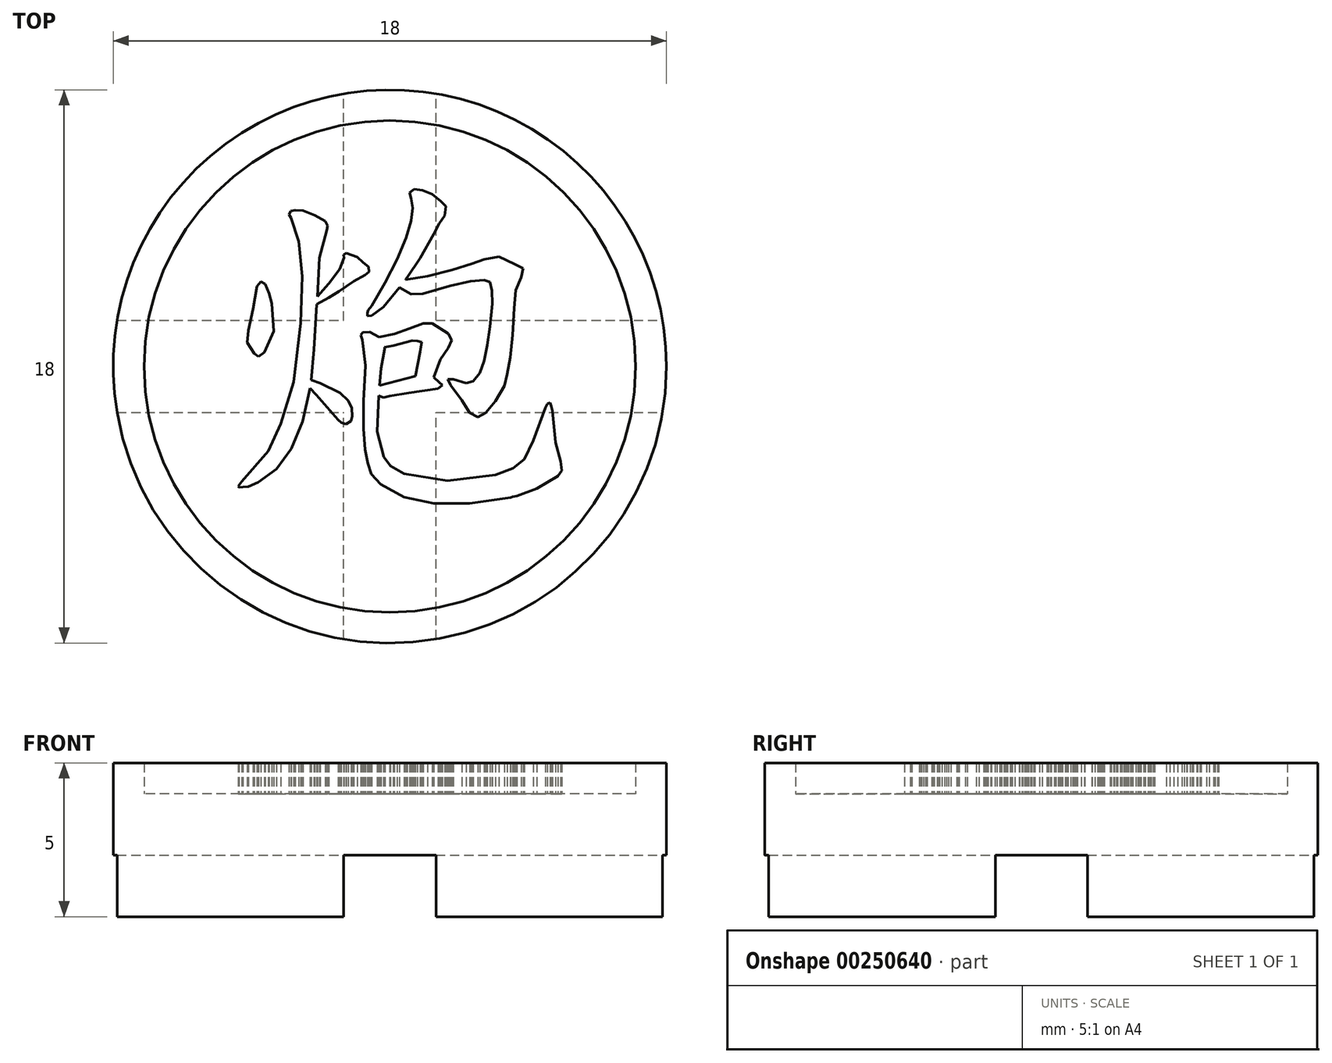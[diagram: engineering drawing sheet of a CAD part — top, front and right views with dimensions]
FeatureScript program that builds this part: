
annotation { "Feature Type Name" : "Feature", "Feature Type Description" : "" }
export const myFeature = defineFeature(function(context is Context, id is Id, definition is map)
    precondition{}
    {
        {
            var Q0;
            Q0=qCreatedBy(makeId("Top.planeOp"),FACE);
            var sketch = newSketch(context, id + "F0", { "sketchPlane" : qUnion([Q0])});
            skCircle(sketch, "E0", {"center": v(-31.33, 19.76) * mm, "radius": 9 * mm});
            skSolve(sketch);
        }
        {
            var Q0;
            Q0=qSketchRegion(id+"F0",true);
            extrude(context, id + "F1", {"entities" : qUnion([Q0]), "depth" : 4 * mm});
        }
        {
            var Q0;
            Q0=makeQuery(id+"F1.opExtrude","CAP_FACE",FACE,{"disambiguationData":[OSD([sQuery(id+"F0.wireOp",EDGE,"E0")])],"isStart":false});
            var sketch = newSketch(context, id + "F2", { "sketchPlane" : qUnion([Q0])});
            skCircle(sketch, "E1", {"center": v(-31.33, 19.76) * mm, "radius": 8 * mm});
            skCircle(sketch, "E2", {"center": v(-31.33, 19.76) * mm, "radius": 9 * mm});
            skSolve(sketch);
        }
        {
            var Q0;
            Q0=makeQuery(id+"F1.opExtrude","CAP_FACE",FACE,{"disambiguationData":[OSD([sQuery(id+"F0.wireOp",EDGE,"E0")])],"isStart":true});
            var sketch = newSketch(context, id + "F3", { "sketchPlane" : qUnion([Q0])});
            skLineSegment(sketch, "E3", {"start": v(-31.33, -19.76) * mm, "end": v(-22.33, -19.76) * mm, "construction": true});
            skLineSegment(sketch, "E4", {"start": v(-31.33, -19.76) * mm, "end": v(-31.33, -10.76) * mm, "construction": true});
            skLineSegment(sketch, "E5", {"start": v(-31.33, -19.76) * mm, "end": v(-40.33, -19.76) * mm, "construction": true});
            skLineSegment(sketch, "E6", {"start": v(-31.33, -19.76) * mm, "end": v(-31.33, -28.76) * mm, "construction": true});
            skLineSegment(sketch, "E7.bottom", {"start": v(-40.33, -28.76) * mm, "end": v(-22.33, -28.76) * mm});
            skLineSegment(sketch, "E7.top", {"start": v(-40.33, -10.76) * mm, "end": v(-22.33, -10.76) * mm});
            skLineSegment(sketch, "E7.left", {"start": v(-22.33, -10.76) * mm, "end": v(-22.33, -28.76) * mm});
            skLineSegment(sketch, "E7.right", {"start": v(-40.33, -10.76) * mm, "end": v(-40.33, -28.76) * mm});
            skPoint(sketch, "E8", {"position": v(-31.33, -28.76) * mm});
            skPoint(sketch, "E9", {"position": v(-40.33, -19.76) * mm});
            skPoint(sketch, "E10", {"position": v(-22.33, -19.76) * mm});
            skPoint(sketch, "E11", {"position": v(-31.33, -10.76) * mm});
            skLineSegment(sketch, "E12.bottom", {"start": v(-32.83, -10.76) * mm, "end": v(-29.83, -10.76) * mm});
            skLineSegment(sketch, "E12.top", {"start": v(-32.83, -28.76) * mm, "end": v(-29.83, -28.76) * mm});
            skLineSegment(sketch, "E12.left", {"start": v(-32.83, -10.76) * mm, "end": v(-32.83, -28.76) * mm});
            skLineSegment(sketch, "E12.right", {"start": v(-29.83, -10.76) * mm, "end": v(-29.83, -28.76) * mm});
            skLineSegment(sketch, "E13.bottom", {"start": v(-40.33, -18.26) * mm, "end": v(-22.33, -18.26) * mm});
            skLineSegment(sketch, "E13.top", {"start": v(-40.33, -21.26) * mm, "end": v(-22.33, -21.26) * mm});
            skLineSegment(sketch, "E13.left", {"start": v(-40.33, -18.26) * mm, "end": v(-40.33, -21.26) * mm});
            skLineSegment(sketch, "E13.right", {"start": v(-22.33, -18.26) * mm, "end": v(-22.33, -21.26) * mm});
            skSolve(sketch);
        }
        {
            var Q0;
            {var subQ1=sQuery(id+"F3.wireOp",EDGE,"E12.bottom");var subQ3=makeQuery(id+"F1.opExtrude","CAP_EDGE",EDGE,{"disambiguationData":[OSD([sQuery(id+"F0.wireOp",EDGE,"E0")])],"isStart":true});var subQ4=makeQuery(id+"F3.imprint","INTERSECT",VERTEX,{"derivedFrom":[subQ3,subQ1]});Q0=makeQuery(id+"F3.imprint","IMPRINT",FACE,{"disambiguationData":[TD([[makeQuery(id+"F3.imprint","IMPRINT",EDGE,{"disambiguationData":[TD([[subQ4,1.0]])],"derivedFrom":subQ3}),1.0]])]});}
            var Q1;
            {var subQ1=sQuery(id+"F3.wireOp",EDGE,"E12.bottom");var subQ3=makeQuery(id+"F1.opExtrude","CAP_EDGE",EDGE,{"disambiguationData":[OSD([sQuery(id+"F0.wireOp",EDGE,"E0")])],"isStart":true});var subQ4=makeQuery(id+"F3.imprint","INTERSECT",VERTEX,{"derivedFrom":[subQ3,subQ1]});Q1=makeQuery(id+"F3.imprint","IMPRINT",FACE,{"disambiguationData":[TD([[makeQuery(id+"F3.imprint","IMPRINT",EDGE,{"disambiguationData":[TD([[subQ4,-1.0]])],"derivedFrom":subQ3}),1.0]])]});}
            var Q2;
            {var subQ1=sQuery(id+"F3.wireOp",EDGE,"E12.top");var subQ3=makeQuery(id+"F1.opExtrude","CAP_EDGE",EDGE,{"disambiguationData":[OSD([sQuery(id+"F0.wireOp",EDGE,"E0")])],"isStart":true});var subQ4=makeQuery(id+"F3.imprint","INTERSECT",VERTEX,{"derivedFrom":[subQ3,subQ1]});Q2=makeQuery(id+"F3.imprint","IMPRINT",FACE,{"disambiguationData":[TD([[makeQuery(id+"F3.imprint","IMPRINT",EDGE,{"disambiguationData":[TD([[subQ4,-1.0]])],"derivedFrom":subQ3}),1.0]])]});}
            var Q3;
            {var subQ1=sQuery(id+"F3.wireOp",EDGE,"E12.top");var subQ3=makeQuery(id+"F1.opExtrude","CAP_EDGE",EDGE,{"disambiguationData":[OSD([sQuery(id+"F0.wireOp",EDGE,"E0")])],"isStart":true});var subQ4=makeQuery(id+"F3.imprint","INTERSECT",VERTEX,{"derivedFrom":[subQ3,subQ1]});Q3=makeQuery(id+"F3.imprint","IMPRINT",FACE,{"disambiguationData":[TD([[makeQuery(id+"F3.imprint","IMPRINT",EDGE,{"disambiguationData":[TD([[subQ4,1.0]])],"derivedFrom":subQ3}),1.0]])]});}
            var Q4;
            {var subQ0=sQuery(id+"F3.wireOp",EDGE,"E13.left");var subQ3=makeQuery(id+"F1.opExtrude","CAP_EDGE",EDGE,{"disambiguationData":[OSD([sQuery(id+"F0.wireOp",EDGE,"E0")])],"isStart":true});var subQ5=makeQuery(id+"F3.imprint","INTERSECT",VERTEX,{"derivedFrom":[subQ3,subQ0]});Q4=makeQuery(id+"F3.imprint","IMPRINT",FACE,{"disambiguationData":[TD([[makeQuery(id+"F3.imprint","IMPRINT",EDGE,{"disambiguationData":[TD([[subQ5,-1.0]])],"derivedFrom":subQ3}),1.0]])]});}
            var Q5;
            {var subQ0=sQuery(id+"F3.wireOp",EDGE,"E13.right");var subQ3=makeQuery(id+"F1.opExtrude","CAP_EDGE",EDGE,{"disambiguationData":[OSD([sQuery(id+"F0.wireOp",EDGE,"E0")])],"isStart":true});var subQ5=makeQuery(id+"F3.imprint","INTERSECT",VERTEX,{"derivedFrom":[subQ3,subQ0]});Q5=makeQuery(id+"F3.imprint","IMPRINT",FACE,{"disambiguationData":[TD([[makeQuery(id+"F3.imprint","IMPRINT",EDGE,{"disambiguationData":[TD([[subQ5,1.0]])],"derivedFrom":subQ3}),1.0]])]});}
            var Q6;
            {var subQ0=sQuery(id+"F3.wireOp",EDGE,"E13.left");var subQ3=makeQuery(id+"F1.opExtrude","CAP_EDGE",EDGE,{"disambiguationData":[OSD([sQuery(id+"F0.wireOp",EDGE,"E0")])],"isStart":true});var subQ5=makeQuery(id+"F3.imprint","INTERSECT",VERTEX,{"derivedFrom":[subQ3,subQ0]});Q6=makeQuery(id+"F3.imprint","IMPRINT",FACE,{"disambiguationData":[TD([[makeQuery(id+"F3.imprint","IMPRINT",EDGE,{"disambiguationData":[TD([[subQ5,1.0]])],"derivedFrom":subQ3}),1.0]])]});}
            var Q7;
            {var subQ0=sQuery(id+"F3.wireOp",EDGE,"E13.right");var subQ3=makeQuery(id+"F1.opExtrude","CAP_EDGE",EDGE,{"disambiguationData":[OSD([sQuery(id+"F0.wireOp",EDGE,"E0")])],"isStart":true});var subQ5=makeQuery(id+"F3.imprint","INTERSECT",VERTEX,{"derivedFrom":[subQ3,subQ0]});Q7=makeQuery(id+"F3.imprint","IMPRINT",FACE,{"disambiguationData":[TD([[makeQuery(id+"F3.imprint","IMPRINT",EDGE,{"disambiguationData":[TD([[subQ5,-1.0]])],"derivedFrom":subQ3}),1.0]])]});}
            var Q8;
            {var subQ3=makeQuery(id+"F1.opExtrude","CAP_EDGE",EDGE,{"disambiguationData":[OSD([sQuery(id+"F0.wireOp",EDGE,"E0")])],"isStart":true});var subQ5=sQuery(id+"F3.wireOp",EDGE,"E12.left");var subQ8=makeQuery(id+"F3.imprint","INTERSECT",VERTEX,{"disambiguationData":[OD(1.0)],"derivedFrom":[subQ3,subQ5]});Q8=makeQuery(id+"F3.imprint","IMPRINT",FACE,{"disambiguationData":[TD([[makeQuery(id+"F3.imprint","IMPRINT",EDGE,{"disambiguationData":[TD([[subQ8,-1.0]])],"derivedFrom":subQ3}),1.0]])]});}
            var Q9;
            {var subQ3=makeQuery(id+"F1.opExtrude","CAP_EDGE",EDGE,{"disambiguationData":[OSD([sQuery(id+"F0.wireOp",EDGE,"E0")])],"isStart":true});var subQ5=sQuery(id+"F3.wireOp",EDGE,"E12.right");var subQ8=makeQuery(id+"F3.imprint","INTERSECT",VERTEX,{"disambiguationData":[OD(1.0)],"derivedFrom":[subQ3,subQ5]});Q9=makeQuery(id+"F3.imprint","IMPRINT",FACE,{"disambiguationData":[TD([[makeQuery(id+"F3.imprint","IMPRINT",EDGE,{"disambiguationData":[TD([[subQ8,1.0]])],"derivedFrom":subQ3}),1.0]])]});}
            var Q10;
            {var subQ3=makeQuery(id+"F1.opExtrude","CAP_EDGE",EDGE,{"disambiguationData":[OSD([sQuery(id+"F0.wireOp",EDGE,"E0")])],"isStart":true});var subQ5=sQuery(id+"F3.wireOp",EDGE,"E12.left");var subQ8=makeQuery(id+"F3.imprint","INTERSECT",VERTEX,{"disambiguationData":[OD(0.0)],"derivedFrom":[subQ3,subQ5]});Q10=makeQuery(id+"F3.imprint","IMPRINT",FACE,{"disambiguationData":[TD([[makeQuery(id+"F3.imprint","IMPRINT",EDGE,{"disambiguationData":[TD([[subQ8,1.0]])],"derivedFrom":subQ3}),1.0]])]});}
            var Q11;
            {var subQ3=makeQuery(id+"F1.opExtrude","CAP_EDGE",EDGE,{"disambiguationData":[OSD([sQuery(id+"F0.wireOp",EDGE,"E0")])],"isStart":true});var subQ5=sQuery(id+"F3.wireOp",EDGE,"E12.right");var subQ8=makeQuery(id+"F3.imprint","INTERSECT",VERTEX,{"disambiguationData":[OD(0.0)],"derivedFrom":[subQ3,subQ5]});Q11=makeQuery(id+"F3.imprint","IMPRINT",FACE,{"disambiguationData":[TD([[makeQuery(id+"F3.imprint","IMPRINT",EDGE,{"disambiguationData":[TD([[subQ8,-1.0]])],"derivedFrom":subQ3}),1.0]])]});}
            var Q12;
            {var subQ2=sQuery(id+"F3.wireOp",EDGE,"E12.left");var subQ4=sQuery(id+"F3.wireOp",EDGE,"E13.bottom");var subQ8=makeQuery(id+"F3.imprint","INTERSECT",VERTEX,{"derivedFrom":[subQ2,subQ4]});Q12=makeQuery(id+"F3.imprint","IMPRINT",FACE,{"disambiguationData":[TD([[makeQuery(id+"F3.imprint","IMPRINT",EDGE,{"disambiguationData":[TD([[subQ8,1.0]])],"derivedFrom":subQ2}),1.0]])]});}
            var Q13;
            {var subQ1=sQuery(id+"F3.wireOp",EDGE,"E12.left");var subQ5=sQuery(id+"F3.wireOp",EDGE,"E13.bottom");var subQ6=makeQuery(id+"F3.imprint","INTERSECT",VERTEX,{"derivedFrom":[subQ1,subQ5]});Q13=makeQuery(id+"F3.imprint","IMPRINT",FACE,{"disambiguationData":[TD([[makeQuery(id+"F3.imprint","IMPRINT",EDGE,{"disambiguationData":[TD([[subQ6,-1.0]])],"derivedFrom":subQ1}),-1.0]])]});}
            var Q14;
            {var subQ0=sQuery(id+"F3.wireOp",EDGE,"E13.top");var subQ1=sQuery(id+"F3.wireOp",EDGE,"E12.left");var subQ2=makeQuery(id+"F3.imprint","INTERSECT",VERTEX,{"derivedFrom":[subQ1,subQ0]});Q14=makeQuery(id+"F3.imprint","IMPRINT",FACE,{"disambiguationData":[TD([[makeQuery(id+"F3.imprint","IMPRINT",EDGE,{"disambiguationData":[TD([[subQ2,-1.0]])],"derivedFrom":subQ1}),1.0]])]});}
            var Q15;
            {var subQ2=sQuery(id+"F3.wireOp",EDGE,"E13.bottom");var subQ5=sQuery(id+"F3.wireOp",EDGE,"E12.right");var subQ8=makeQuery(id+"F3.imprint","INTERSECT",VERTEX,{"derivedFrom":[subQ5,subQ2]});Q15=makeQuery(id+"F3.imprint","IMPRINT",FACE,{"disambiguationData":[TD([[makeQuery(id+"F3.imprint","IMPRINT",EDGE,{"disambiguationData":[TD([[subQ8,-1.0]])],"derivedFrom":subQ5}),1.0]])]});}
            var Q16;
            {var subQ0=sQuery(id+"F3.wireOp",EDGE,"E13.bottom");var subQ1=sQuery(id+"F3.wireOp",EDGE,"E12.left");var subQ2=makeQuery(id+"F3.imprint","INTERSECT",VERTEX,{"derivedFrom":[subQ1,subQ0]});Q16=makeQuery(id+"F3.imprint","IMPRINT",FACE,{"disambiguationData":[TD([[makeQuery(id+"F3.imprint","IMPRINT",EDGE,{"disambiguationData":[TD([[subQ2,-1.0]])],"derivedFrom":subQ1}),1.0]])]});}
            extrude(context, id + "F4", {"entities" : qUnion([Q0, Q1, Q2, Q3, Q4, Q5, Q6, Q7, Q8, Q9, Q10, Q11, Q12, Q13, Q14, Q15, Q16]), "operationType" : NewBodyOperationType.REMOVE, "oppositeDirection" : true, "depth" : 2 * mm});
        }
        {
            var Q0;
            Q0=qSketchRegion(id+"F2",true);
            var Q1;
            Q1=makeQuery(id+"F2.imprint","IMPRINT",FACE,{"disambiguationData":[TD([[makeQuery(id+"F2.imprint","IMPRINT",EDGE,{"derivedFrom":sQuery(id+"F2.wireOp",EDGE,"hKqnuJLd-dfdz-vJIs-yDKo-c4hLNRw30SuP")}),-1.0]])]});
            extrude(context, id + "F5", {"entities" : qUnion([Q0, Q1]), "operationType" : NewBodyOperationType.ADD, "depth" : 1 * mm});
        }
        {
            var Q0;
            Q0=makeQuery(id+"F1.opExtrude","CAP_FACE",FACE,{"disambiguationData":[OSD([sQuery(id+"F0.wireOp",EDGE,"E0")])],"isStart":false});
            var sketch = newSketch(context, id + "F6", { "sketchPlane" : qUnion([Q0])});
            skLineSegment(sketch, "E14", {"start": v(-31.01, 22.32) * mm, "end": v(-30.64, 22.11) * mm});
            skLineSegment(sketch, "E15", {"start": v(-30.64, 22.11) * mm, "end": v(-30.26, 22.13) * mm});
            skLineSegment(sketch, "E16", {"start": v(-30.26, 22.13) * mm, "end": v(-29.38, 22.38) * mm});
            skLineSegment(sketch, "E17", {"start": v(-29.38, 22.38) * mm, "end": v(-28.7, 22.53) * mm});
            skLineSegment(sketch, "E18", {"start": v(-28.7, 22.53) * mm, "end": v(-28.27, 22.57) * mm});
            skLineSegment(sketch, "E19", {"start": v(-28.27, 22.57) * mm, "end": v(-28.07, 22.5) * mm});
            skLineSegment(sketch, "E20", {"start": v(-28.07, 22.5) * mm, "end": v(-28.01, 22.22) * mm});
            skLineSegment(sketch, "E21", {"start": v(-28.01, 22.22) * mm, "end": v(-28, 21.8) * mm});
            skLineSegment(sketch, "E22", {"start": v(-28, 21.8) * mm, "end": v(-28.08, 21.06) * mm});
            skLineSegment(sketch, "E23", {"start": v(-28.08, 21.06) * mm, "end": v(-28.16, 20.44) * mm});
            skLineSegment(sketch, "E24", {"start": v(-28.16, 20.44) * mm, "end": v(-28.26, 19.95) * mm});
            skLineSegment(sketch, "E25", {"start": v(-28.26, 19.95) * mm, "end": v(-28.4, 19.55) * mm});
            skLineSegment(sketch, "E26", {"start": v(-28.4, 19.55) * mm, "end": v(-28.61, 19.28) * mm});
            skLineSegment(sketch, "E27", {"start": v(-28.61, 19.28) * mm, "end": v(-28.85, 19.22) * mm});
            skLineSegment(sketch, "E28", {"start": v(-28.85, 19.22) * mm, "end": v(-29.26, 19.34) * mm});
            skLineSegment(sketch, "E29", {"start": v(-29.26, 19.34) * mm, "end": v(-29.45, 19.34) * mm});
            skLineSegment(sketch, "E30", {"start": v(-29.45, 19.34) * mm, "end": v(-29.36, 19.15) * mm});
            skLineSegment(sketch, "E31", {"start": v(-29.36, 19.15) * mm, "end": v(-28.99, 18.65) * mm});
            skLineSegment(sketch, "E32", {"start": v(-28.99, 18.65) * mm, "end": v(-28.73, 18.25) * mm});
            skLineSegment(sketch, "E33", {"start": v(-28.73, 18.25) * mm, "end": v(-28.46, 18.1) * mm});
            skLineSegment(sketch, "E34", {"start": v(-28.46, 18.1) * mm, "end": v(-28.22, 18.25) * mm});
            skLineSegment(sketch, "E35", {"start": v(-28.22, 18.25) * mm, "end": v(-27.9, 18.63) * mm});
            skLineSegment(sketch, "E36", {"start": v(-27.9, 18.63) * mm, "end": v(-27.6, 19.12) * mm});
            skLineSegment(sketch, "E37", {"start": v(-27.6, 19.12) * mm, "end": v(-27.51, 19.5) * mm});
            skLineSegment(sketch, "E38", {"start": v(-27.51, 19.5) * mm, "end": v(-27.42, 20.06) * mm});
            skLineSegment(sketch, "E39", {"start": v(-27.42, 20.06) * mm, "end": v(-27.34, 20.78) * mm});
            skLineSegment(sketch, "E40", {"start": v(-27.34, 20.78) * mm, "end": v(-27.3, 21.66) * mm});
            skLineSegment(sketch, "E41", {"start": v(-27.3, 21.66) * mm, "end": v(-27.24, 22.24) * mm});
            skLineSegment(sketch, "E42", {"start": v(-27.24, 22.24) * mm, "end": v(-27.06, 22.66) * mm});
            skLineSegment(sketch, "E43", {"start": v(-27.06, 22.66) * mm, "end": v(-27, 22.95) * mm});
            skLineSegment(sketch, "E44", {"start": v(-27, 22.95) * mm, "end": v(-27.28, 23.1) * mm});
            skLineSegment(sketch, "E45", {"start": v(-27.28, 23.1) * mm, "end": v(-27.78, 23.33) * mm});
            skLineSegment(sketch, "E46", {"start": v(-27.78, 23.33) * mm, "end": v(-28.26, 23.24) * mm});
            skLineSegment(sketch, "E47", {"start": v(-28.26, 23.24) * mm, "end": v(-28.65, 23.1) * mm});
            skLineSegment(sketch, "E48", {"start": v(-28.65, 23.1) * mm, "end": v(-29.31, 22.9) * mm});
            skLineSegment(sketch, "E49", {"start": v(-29.31, 22.9) * mm, "end": v(-30.1, 22.7) * mm});
            skLineSegment(sketch, "E50", {"start": v(-30.1, 22.7) * mm, "end": v(-30.82, 22.58) * mm});
            skLineSegment(sketch, "E51", {"start": v(-30.82, 22.58) * mm, "end": v(-30.82, 22.6) * mm});
            skLineSegment(sketch, "E52", {"start": v(-30.82, 22.6) * mm, "end": v(-30.77, 22.65) * mm});
            skLineSegment(sketch, "E53", {"start": v(-30.77, 22.65) * mm, "end": v(-30.35, 23.28) * mm});
            skLineSegment(sketch, "E54", {"start": v(-30.35, 23.28) * mm, "end": v(-29.9, 24.06) * mm});
            skLineSegment(sketch, "E55", {"start": v(-29.9, 24.06) * mm, "end": v(-29.73, 24.4) * mm});
            skLineSegment(sketch, "E56", {"start": v(-29.73, 24.4) * mm, "end": v(-29.54, 24.66) * mm});
            skLineSegment(sketch, "E57", {"start": v(-29.54, 24.66) * mm, "end": v(-29.5, 24.96) * mm});
            skLineSegment(sketch, "E58", {"start": v(-29.5, 24.96) * mm, "end": v(-29.67, 25.13) * mm});
            skLineSegment(sketch, "E59", {"start": v(-29.67, 25.13) * mm, "end": v(-29.96, 25.37) * mm});
            skLineSegment(sketch, "E60", {"start": v(-29.96, 25.37) * mm, "end": v(-30.28, 25.49) * mm});
            skLineSegment(sketch, "E61", {"start": v(-30.28, 25.49) * mm, "end": v(-30.54, 25.52) * mm});
            skLineSegment(sketch, "E62", {"start": v(-30.54, 25.52) * mm, "end": v(-30.69, 25.41) * mm});
            skLineSegment(sketch, "E63", {"start": v(-30.69, 25.41) * mm, "end": v(-30.64, 25.22) * mm});
            skLineSegment(sketch, "E64", {"start": v(-30.64, 25.22) * mm, "end": v(-30.6, 24.92) * mm});
            skLineSegment(sketch, "E65", {"start": v(-30.6, 24.92) * mm, "end": v(-30.64, 24.5) * mm});
            skLineSegment(sketch, "E66", {"start": v(-30.64, 24.5) * mm, "end": v(-30.8, 23.94) * mm});
            skLineSegment(sketch, "E67", {"start": v(-30.8, 23.94) * mm, "end": v(-31.1, 23.24) * mm});
            skLineSegment(sketch, "E68", {"start": v(-31.1, 23.24) * mm, "end": v(-31.49, 22.48) * mm});
            skLineSegment(sketch, "E69", {"start": v(-31.49, 22.48) * mm, "end": v(-31.92, 21.73) * mm});
            skLineSegment(sketch, "E70", {"start": v(-31.92, 21.73) * mm, "end": v(-32.03, 21.59) * mm});
            skLineSegment(sketch, "E71", {"start": v(-32.03, 21.59) * mm, "end": v(-32.06, 21.5) * mm});
            skLineSegment(sketch, "E72", {"start": v(-32.06, 21.5) * mm, "end": v(-32.06, 21.4) * mm});
            skLineSegment(sketch, "E73", {"start": v(-32.06, 21.4) * mm, "end": v(-31.91, 21.41) * mm});
            skLineSegment(sketch, "E74", {"start": v(-31.91, 21.41) * mm, "end": v(-31.54, 21.7) * mm});
            skLineSegment(sketch, "E75", {"start": v(-31.54, 21.7) * mm, "end": v(-31.01, 22.32) * mm});
            skLineSegment(sketch, "E76", {"start": v(-31.68, 20.72) * mm, "end": v(-31.99, 20.88) * mm});
            skLineSegment(sketch, "E77", {"start": v(-31.99, 20.88) * mm, "end": v(-32.22, 20.86) * mm});
            skLineSegment(sketch, "E78", {"start": v(-32.22, 20.86) * mm, "end": v(-32.28, 20.78) * mm});
            skLineSegment(sketch, "E79", {"start": v(-32.28, 20.78) * mm, "end": v(-32.23, 20.63) * mm});
            skLineSegment(sketch, "E80", {"start": v(-32.23, 20.63) * mm, "end": v(-32.12, 19.8) * mm});
            skLineSegment(sketch, "E81", {"start": v(-32.12, 19.8) * mm, "end": v(-32.18, 18.64) * mm});
            skLineSegment(sketch, "E82", {"start": v(-32.18, 18.64) * mm, "end": v(-32.19, 17.73) * mm});
            skLineSegment(sketch, "E83", {"start": v(-32.19, 17.73) * mm, "end": v(-32.14, 17.06) * mm});
            skLineSegment(sketch, "E84", {"start": v(-32.14, 17.06) * mm, "end": v(-32.05, 16.62) * mm});
            skLineSegment(sketch, "E85", {"start": v(-32.05, 16.62) * mm, "end": v(-31.94, 16.25) * mm});
            skLineSegment(sketch, "E86", {"start": v(-31.94, 16.25) * mm, "end": v(-31.62, 15.92) * mm});
            skLineSegment(sketch, "E87", {"start": v(-31.62, 15.92) * mm, "end": v(-30.86, 15.5) * mm});
            skLineSegment(sketch, "E88", {"start": v(-30.86, 15.5) * mm, "end": v(-29.9, 15.3) * mm});
            skLineSegment(sketch, "E89", {"start": v(-29.9, 15.3) * mm, "end": v(-28.74, 15.3) * mm});
            skLineSegment(sketch, "E90", {"start": v(-28.74, 15.3) * mm, "end": v(-27.4, 15.5) * mm});
            skLineSegment(sketch, "E91", {"start": v(-27.4, 15.5) * mm, "end": v(-27.33, 15.52) * mm});
            skLineSegment(sketch, "E92", {"start": v(-27.33, 15.52) * mm, "end": v(-27.2, 15.55) * mm});
            skLineSegment(sketch, "E93", {"start": v(-27.2, 15.55) * mm, "end": v(-26.55, 15.79) * mm});
            skLineSegment(sketch, "E94", {"start": v(-26.55, 15.79) * mm, "end": v(-25.87, 16.19) * mm});
            skLineSegment(sketch, "E95", {"start": v(-25.87, 16.19) * mm, "end": v(-25.74, 16.37) * mm});
            skLineSegment(sketch, "E96", {"start": v(-25.74, 16.37) * mm, "end": v(-25.77, 16.68) * mm});
            skLineSegment(sketch, "E97", {"start": v(-25.77, 16.68) * mm, "end": v(-25.93, 17.29) * mm});
            skLineSegment(sketch, "E98", {"start": v(-25.93, 17.29) * mm, "end": v(-26.04, 18.32) * mm});
            skLineSegment(sketch, "E99", {"start": v(-26.04, 18.32) * mm, "end": v(-26.08, 18.47) * mm});
            skLineSegment(sketch, "E100", {"start": v(-26.08, 18.47) * mm, "end": v(-26.12, 18.59) * mm});
            skLineSegment(sketch, "E101", {"start": v(-26.12, 18.59) * mm, "end": v(-26.2, 18.55) * mm});
            skLineSegment(sketch, "E102", {"start": v(-26.2, 18.55) * mm, "end": v(-26.27, 18.42) * mm});
            skLineSegment(sketch, "E103", {"start": v(-26.27, 18.42) * mm, "end": v(-26.66, 17.35) * mm});
            skLineSegment(sketch, "E104", {"start": v(-26.66, 17.35) * mm, "end": v(-26.95, 16.74) * mm});
            skLineSegment(sketch, "E105", {"start": v(-26.95, 16.74) * mm, "end": v(-27.32, 16.44) * mm});
            skLineSegment(sketch, "E106", {"start": v(-27.32, 16.44) * mm, "end": v(-27.9, 16.24) * mm});
            skLineSegment(sketch, "E107", {"start": v(-27.9, 16.24) * mm, "end": v(-29.45, 16.04) * mm});
            skLineSegment(sketch, "E108", {"start": v(-29.45, 16.04) * mm, "end": v(-30.87, 16.27) * mm});
            skLineSegment(sketch, "E109", {"start": v(-30.87, 16.27) * mm, "end": v(-31.3, 16.52) * mm});
            skLineSegment(sketch, "E110", {"start": v(-31.3, 16.52) * mm, "end": v(-31.53, 16.82) * mm});
            skLineSegment(sketch, "E111", {"start": v(-31.53, 16.82) * mm, "end": v(-31.74, 17.65) * mm});
            skLineSegment(sketch, "E112", {"start": v(-31.74, 17.65) * mm, "end": v(-31.7, 18.8) * mm});
            skLineSegment(sketch, "E113", {"start": v(-31.7, 18.8) * mm, "end": v(-31.54, 18.74) * mm});
            skLineSegment(sketch, "E114", {"start": v(-31.54, 18.74) * mm, "end": v(-31.34, 18.8) * mm});
            skLineSegment(sketch, "E115", {"start": v(-31.34, 18.8) * mm, "end": v(-30.71, 18.9) * mm});
            skLineSegment(sketch, "E116", {"start": v(-30.71, 18.9) * mm, "end": v(-29.76, 19.04) * mm});
            skLineSegment(sketch, "E117", {"start": v(-29.76, 19.04) * mm, "end": v(-29.63, 19.16) * mm});
            skLineSegment(sketch, "E118", {"start": v(-29.63, 19.16) * mm, "end": v(-29.72, 19.25) * mm});
            skLineSegment(sketch, "E119", {"start": v(-29.72, 19.25) * mm, "end": v(-29.9, 19.4) * mm});
            skLineSegment(sketch, "E120", {"start": v(-29.9, 19.4) * mm, "end": v(-29.68, 20) * mm});
            skLineSegment(sketch, "E121", {"start": v(-29.68, 20) * mm, "end": v(-29.43, 20.36) * mm});
            skLineSegment(sketch, "E122", {"start": v(-29.43, 20.36) * mm, "end": v(-29.32, 20.6) * mm});
            skLineSegment(sketch, "E123", {"start": v(-29.32, 20.6) * mm, "end": v(-29.43, 20.83) * mm});
            skLineSegment(sketch, "E124", {"start": v(-29.43, 20.83) * mm, "end": v(-29.96, 21.16) * mm});
            skLineSegment(sketch, "E125", {"start": v(-29.96, 21.16) * mm, "end": v(-30.25, 21.16) * mm});
            skLineSegment(sketch, "E126", {"start": v(-30.25, 21.16) * mm, "end": v(-30.68, 21) * mm});
            skLineSegment(sketch, "E127", {"start": v(-30.68, 21) * mm, "end": v(-31.18, 20.81) * mm});
            skLineSegment(sketch, "E128", {"start": v(-31.18, 20.81) * mm, "end": v(-31.68, 20.72) * mm});
            skLineSegment(sketch, "E129", {"start": v(-31.5, 20.33) * mm, "end": v(-31.5, 20.39) * mm});
            skLineSegment(sketch, "E130", {"start": v(-31.5, 20.39) * mm, "end": v(-31.23, 20.44) * mm});
            skLineSegment(sketch, "E131", {"start": v(-31.23, 20.44) * mm, "end": v(-30.6, 20.6) * mm});
            skLineSegment(sketch, "E132", {"start": v(-30.6, 20.6) * mm, "end": v(-30.43, 20.59) * mm});
            skLineSegment(sketch, "E133", {"start": v(-30.43, 20.59) * mm, "end": v(-30.3, 20.55) * mm});
            skLineSegment(sketch, "E134", {"start": v(-30.3, 20.55) * mm, "end": v(-30.34, 20.24) * mm});
            skLineSegment(sketch, "E135", {"start": v(-30.34, 20.24) * mm, "end": v(-30.5, 19.44) * mm});
            skLineSegment(sketch, "E136", {"start": v(-30.5, 19.44) * mm, "end": v(-31.67, 19.14) * mm});
            skLineSegment(sketch, "E137", {"start": v(-31.67, 19.14) * mm, "end": v(-31.62, 19.7) * mm});
            skLineSegment(sketch, "E138", {"start": v(-31.62, 19.7) * mm, "end": v(-31.5, 20.33) * mm});
            skLineSegment(sketch, "E139", {"start": v(-35.65, 22.37) * mm, "end": v(-35.78, 21.62) * mm});
            skLineSegment(sketch, "E140", {"start": v(-35.78, 21.62) * mm, "end": v(-35.93, 20.94) * mm});
            skLineSegment(sketch, "E141", {"start": v(-35.93, 20.94) * mm, "end": v(-35.97, 20.53) * mm});
            skLineSegment(sketch, "E142", {"start": v(-35.97, 20.53) * mm, "end": v(-35.75, 20.18) * mm});
            skLineSegment(sketch, "E143", {"start": v(-35.75, 20.18) * mm, "end": v(-35.6, 20.08) * mm});
            skLineSegment(sketch, "E144", {"start": v(-35.6, 20.08) * mm, "end": v(-35.4, 20.22) * mm});
            skLineSegment(sketch, "E145", {"start": v(-35.4, 20.22) * mm, "end": v(-35.11, 20.9) * mm});
            skLineSegment(sketch, "E146", {"start": v(-35.11, 20.9) * mm, "end": v(-35.18, 21.81) * mm});
            skLineSegment(sketch, "E147", {"start": v(-35.18, 21.81) * mm, "end": v(-35.26, 22.14) * mm});
            skLineSegment(sketch, "E148", {"start": v(-35.26, 22.14) * mm, "end": v(-35.38, 22.45) * mm});
            skLineSegment(sketch, "E149", {"start": v(-35.38, 22.45) * mm, "end": v(-35.53, 22.52) * mm});
            skLineSegment(sketch, "E150", {"start": v(-35.53, 22.52) * mm, "end": v(-35.65, 22.37) * mm});
            skLineSegment(sketch, "E151", {"start": v(-33.92, 19.05) * mm, "end": v(-33.73, 18.83) * mm});
            skLineSegment(sketch, "E152", {"start": v(-33.73, 18.83) * mm, "end": v(-33, 18.03) * mm});
            skLineSegment(sketch, "E153", {"start": v(-33, 18.03) * mm, "end": v(-32.91, 17.93) * mm});
            skLineSegment(sketch, "E154", {"start": v(-32.91, 17.93) * mm, "end": v(-32.75, 17.88) * mm});
            skLineSegment(sketch, "E155", {"start": v(-32.75, 17.88) * mm, "end": v(-32.6, 17.99) * mm});
            skLineSegment(sketch, "E156", {"start": v(-32.6, 17.99) * mm, "end": v(-32.55, 18.13) * mm});
            skLineSegment(sketch, "E157", {"start": v(-32.55, 18.13) * mm, "end": v(-32.57, 18.4) * mm});
            skLineSegment(sketch, "E158", {"start": v(-32.57, 18.4) * mm, "end": v(-32.69, 18.64) * mm});
            skLineSegment(sketch, "E159", {"start": v(-32.69, 18.64) * mm, "end": v(-32.95, 18.9) * mm});
            skLineSegment(sketch, "E160", {"start": v(-32.95, 18.9) * mm, "end": v(-33.6, 19.22) * mm});
            skLineSegment(sketch, "E161", {"start": v(-33.6, 19.22) * mm, "end": v(-33.88, 19.32) * mm});
            skLineSegment(sketch, "E162", {"start": v(-33.88, 19.32) * mm, "end": v(-33.8, 20.31) * mm});
            skLineSegment(sketch, "E163", {"start": v(-33.8, 20.31) * mm, "end": v(-33.71, 21.78) * mm});
            skLineSegment(sketch, "E164", {"start": v(-33.71, 21.78) * mm, "end": v(-33.32, 22) * mm});
            skLineSegment(sketch, "E165", {"start": v(-33.32, 22) * mm, "end": v(-32.99, 22.2) * mm});
            skLineSegment(sketch, "E166", {"start": v(-32.99, 22.2) * mm, "end": v(-32.5, 22.54) * mm});
            skLineSegment(sketch, "E167", {"start": v(-32.5, 22.54) * mm, "end": v(-32.13, 22.74) * mm});
            skLineSegment(sketch, "E168", {"start": v(-32.13, 22.74) * mm, "end": v(-32, 22.83) * mm});
            skLineSegment(sketch, "E169", {"start": v(-32, 22.83) * mm, "end": v(-32.02, 23) * mm});
            skLineSegment(sketch, "E170", {"start": v(-32.02, 23) * mm, "end": v(-32.2, 23.14) * mm});
            skLineSegment(sketch, "E171", {"start": v(-32.2, 23.14) * mm, "end": v(-32.39, 23.32) * mm});
            skLineSegment(sketch, "E172", {"start": v(-32.39, 23.32) * mm, "end": v(-32.74, 23.44) * mm});
            skLineSegment(sketch, "E173", {"start": v(-32.74, 23.44) * mm, "end": v(-32.83, 23.4) * mm});
            skLineSegment(sketch, "E174", {"start": v(-32.83, 23.4) * mm, "end": v(-32.83, 23.3) * mm});
            skLineSegment(sketch, "E175", {"start": v(-32.83, 23.3) * mm, "end": v(-32.96, 22.93) * mm});
            skLineSegment(sketch, "E176", {"start": v(-32.96, 22.93) * mm, "end": v(-33.31, 22.46) * mm});
            skLineSegment(sketch, "E177", {"start": v(-33.31, 22.46) * mm, "end": v(-33.69, 22.03) * mm});
            skLineSegment(sketch, "E178", {"start": v(-33.69, 22.03) * mm, "end": v(-33.62, 23.29) * mm});
            skLineSegment(sketch, "E179", {"start": v(-33.62, 23.29) * mm, "end": v(-33.38, 24.2) * mm});
            skLineSegment(sketch, "E180", {"start": v(-33.38, 24.2) * mm, "end": v(-33.36, 24.33) * mm});
            skLineSegment(sketch, "E181", {"start": v(-33.36, 24.33) * mm, "end": v(-33.44, 24.49) * mm});
            skLineSegment(sketch, "E182", {"start": v(-33.44, 24.49) * mm, "end": v(-33.77, 24.68) * mm});
            skLineSegment(sketch, "E183", {"start": v(-33.77, 24.68) * mm, "end": v(-34.15, 24.83) * mm});
            skLineSegment(sketch, "E184", {"start": v(-34.15, 24.83) * mm, "end": v(-34.4, 24.84) * mm});
            skLineSegment(sketch, "E185", {"start": v(-34.4, 24.84) * mm, "end": v(-34.54, 24.82) * mm});
            skLineSegment(sketch, "E186", {"start": v(-34.54, 24.82) * mm, "end": v(-34.6, 24.7) * mm});
            skLineSegment(sketch, "E187", {"start": v(-34.6, 24.7) * mm, "end": v(-34.55, 24.6) * mm});
            skLineSegment(sketch, "E188", {"start": v(-34.55, 24.6) * mm, "end": v(-34.3, 23.83) * mm});
            skLineSegment(sketch, "E189", {"start": v(-34.3, 23.83) * mm, "end": v(-34.19, 22.7) * mm});
            skLineSegment(sketch, "E190", {"start": v(-34.19, 22.7) * mm, "end": v(-34.24, 21.17) * mm});
            skLineSegment(sketch, "E191", {"start": v(-34.24, 21.17) * mm, "end": v(-34.46, 19.26) * mm});
            skLineSegment(sketch, "E192", {"start": v(-34.46, 19.26) * mm, "end": v(-34.88, 17.9) * mm});
            skLineSegment(sketch, "E193", {"start": v(-34.88, 17.9) * mm, "end": v(-35.29, 17) * mm});
            skLineSegment(sketch, "E194", {"start": v(-35.29, 17) * mm, "end": v(-36.15, 16.02) * mm});
            skLineSegment(sketch, "E195", {"start": v(-36.15, 16.02) * mm, "end": v(-36.26, 15.86) * mm});
            skLineSegment(sketch, "E196", {"start": v(-36.26, 15.86) * mm, "end": v(-36.24, 15.82) * mm});
            skLineSegment(sketch, "E197", {"start": v(-36.24, 15.82) * mm, "end": v(-36.11, 15.84) * mm});
            skLineSegment(sketch, "E198", {"start": v(-36.11, 15.84) * mm, "end": v(-35.93, 15.85) * mm});
            skLineSegment(sketch, "E199", {"start": v(-35.93, 15.85) * mm, "end": v(-35.62, 16) * mm});
            skLineSegment(sketch, "E200", {"start": v(-35.62, 16) * mm, "end": v(-35.02, 16.42) * mm});
            skLineSegment(sketch, "E201", {"start": v(-35.02, 16.42) * mm, "end": v(-34.53, 17.09) * mm});
            skLineSegment(sketch, "E202", {"start": v(-34.53, 17.09) * mm, "end": v(-34.17, 17.97) * mm});
            skLineSegment(sketch, "E203", {"start": v(-34.17, 17.97) * mm, "end": v(-33.92, 19.05) * mm});
            skSolve(sketch);
        }
        {
            var Q0;
            Q0 = qSketchRegion(id + "F6", true);
            extrude(context, id + "F7", {"entities" : qUnion([Q0]), "operationType" : NewBodyOperationType.ADD, "depth" : 1 * mm, "offsetDistance" : 25 * mm});
        }
    });
